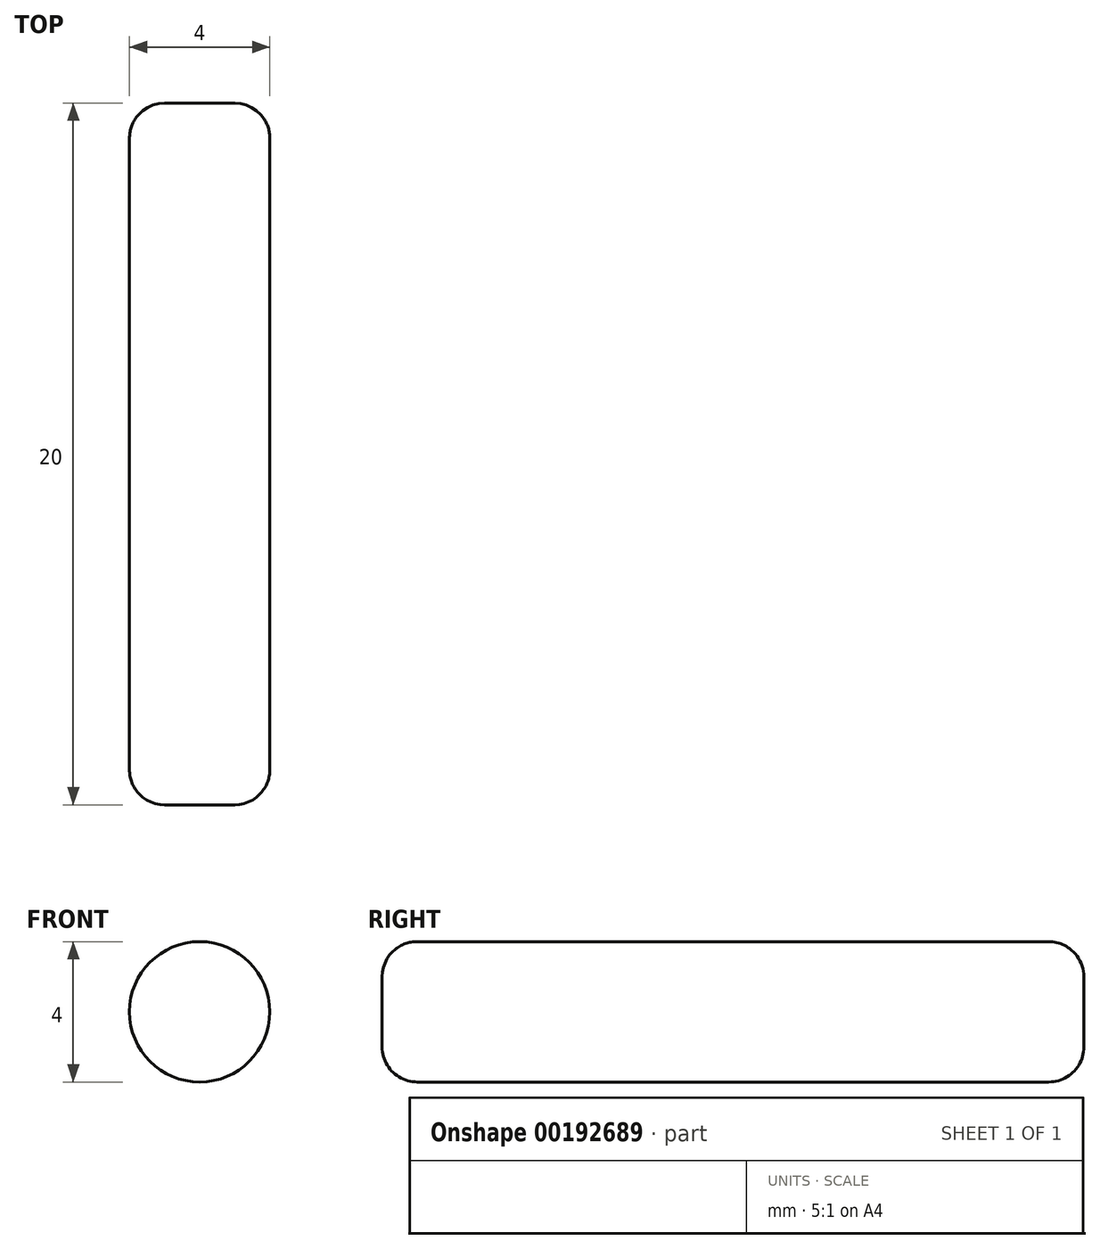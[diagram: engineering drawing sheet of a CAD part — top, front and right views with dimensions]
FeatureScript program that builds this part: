
annotation { "Feature Type Name" : "Feature", "Feature Type Description" : "" }
export const myFeature = defineFeature(function(context is Context, id is Id, definition is map)
    precondition{}
    {
        {
            var Q0;
            Q0=qCreatedBy(makeId("Front.planeOp"),FACE);
            var sketch = newSketch(context, id + "F0", { "sketchPlane" : qUnion([Q0])});
            skCircle(sketch, "E0", {"center": v(0, 0) * mm, "radius": 2 * mm});
            skSolve(sketch);
        }
        {
            var Q0;
            Q0=makeQuery(id+"F0.imprint","IMPRINT",FACE,{"disambiguationData":[TD([[makeQuery(id+"F0.imprint","IMPRINT",EDGE,{"derivedFrom":sQuery(id+"F0.wireOp",EDGE,"E0")}),1.0]])]});
            extrude(context, id + "F1", {"entities" : qUnion([Q0]), "endBound" : BoundingType.SYMMETRIC, "depth" : 20 * mm});
        }
        {
            var Q0;
            Q0=makeQuery(id+"F1.opExtrude","CAP_EDGE",EDGE,{"disambiguationData":[OSD([sQuery(id+"F0.wireOp",EDGE,"E0")])],"isStart":false});
            var Q1;
            Q1=makeQuery(id+"F1.opExtrude","CAP_FACE",FACE,{"disambiguationData":[OSD([sQuery(id+"F0.wireOp",EDGE,"E0")])],"isStart":true});
            fillet(context, id + "F2", {"entities" : qUnion([Q0, Q1]), "radius" : 1 * mm, "tangentPropagation" : true, "allowEdgeOverflow" : false});
        }
    });
